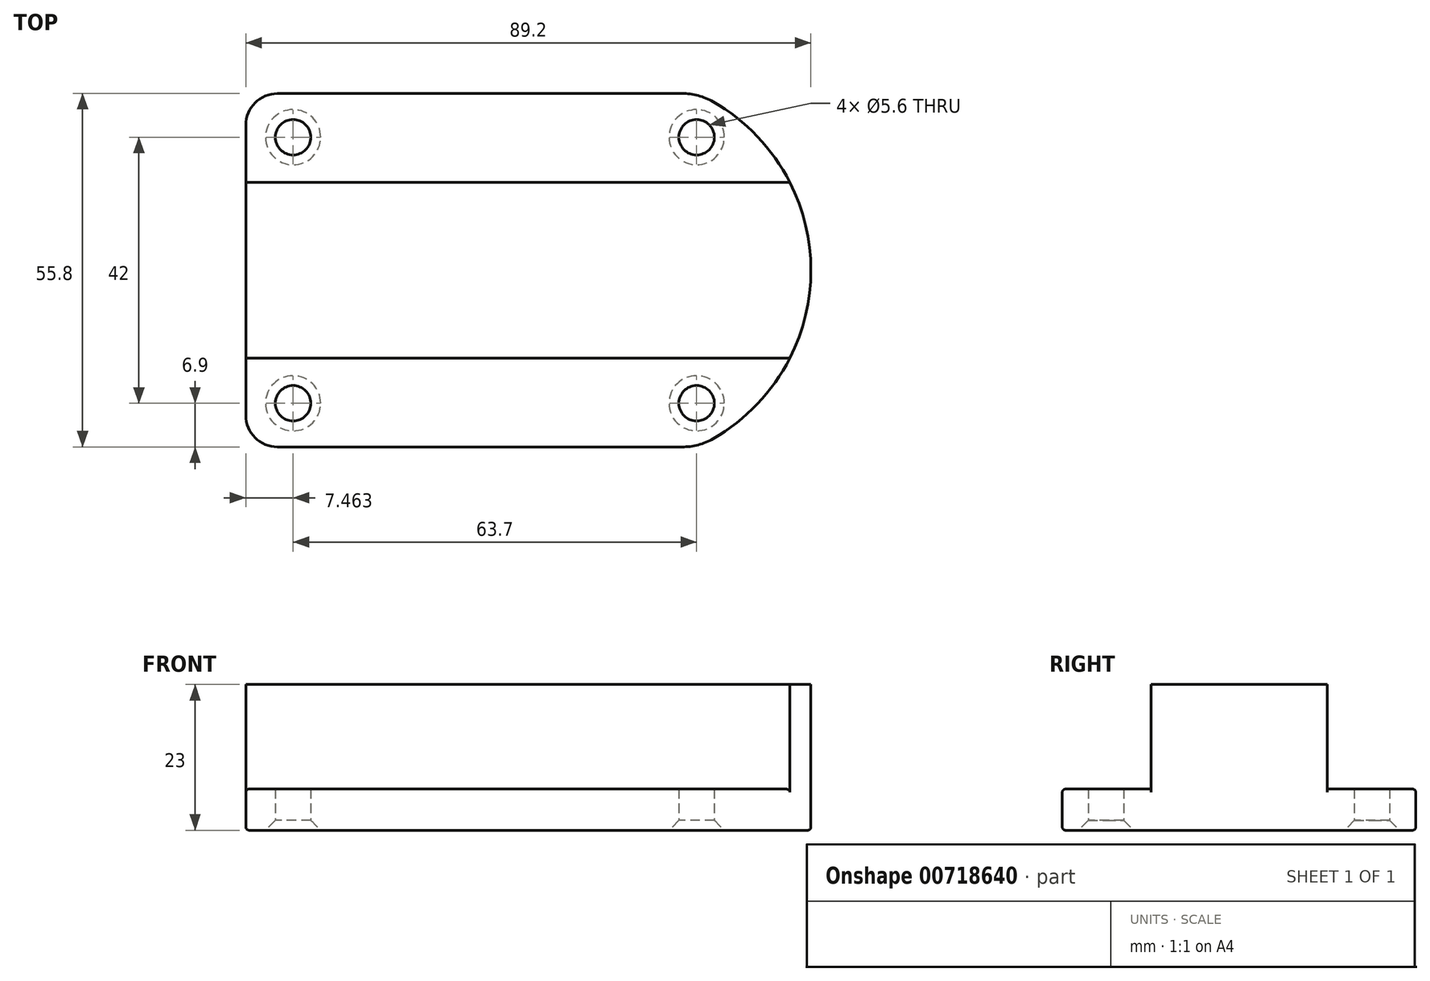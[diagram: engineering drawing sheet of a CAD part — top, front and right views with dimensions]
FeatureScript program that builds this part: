
annotation { "Feature Type Name" : "Feature", "Feature Type Description" : "" }
export const myFeature = defineFeature(function(context is Context, id is Id, definition is map)
    precondition{}
    {
        {
            var Q0;
            Q0=qCreatedBy(makeId("Top.planeOp"),FACE);
            var sketch = newSketch(context, id + "F0", { "sketchPlane" : qUnion([Q0])});
            skLineSegment(sketch, "E0.bottom", {"start": v(-38.88, -28.9) * mm, "end": v(-38.88, 16.9) * mm});
            skLineSegment(sketch, "E0.left", {"start": v(-33.88, -33.9) * mm, "end": v(29.94, -33.9) * mm});
            skLineSegment(sketch, "E0.right", {"start": v(-33.88, 21.9) * mm, "end": v(29.94, 21.9) * mm});
            skArc(sketch, "E1", {"start": v(34.9, -32.58) * mm, "mid": v(50.32, -6) * mm, "end": v(34.9, 20.58) * mm});
            skPoint(sketch, "E2.visualSharp", {"position": v(32.32, 21.9) * mm});
            skArc(sketch, "E2.filletArc", {"start": v(34.9, 20.58) * mm, "mid": v(32.51, 21.56) * mm, "end": v(29.94, 21.9) * mm});
            skPoint(sketch, "E3.visualSharp", {"position": v(32.32, -33.9) * mm});
            skArc(sketch, "E3.filletArc", {"start": v(29.94, -33.9) * mm, "mid": v(32.51, -33.56) * mm, "end": v(34.9, -32.58) * mm});
            skCircle(sketch, "E4", {"center": v(-31.42, 15) * mm, "radius": 2.8 * mm});
            skCircle(sketch, "E5", {"center": v(-31.42, -27) * mm, "radius": 2.8 * mm});
            skCircle(sketch, "E6", {"center": v(32.28, -27) * mm, "radius": 2.8 * mm});
            skCircle(sketch, "E7", {"center": v(32.28, 15) * mm, "radius": 2.8 * mm});
            skPoint(sketch, "E8.visualSharp", {"position": v(-38.88, 21.9) * mm});
            skArc(sketch, "E8.filletArc", {"start": v(-33.88, 21.9) * mm, "mid": v(-37.41, 20.44) * mm, "end": v(-38.88, 16.9) * mm});
            skPoint(sketch, "E9.visualSharp", {"position": v(-38.88, -33.9) * mm});
            skArc(sketch, "E9.filletArc", {"start": v(-38.88, -28.9) * mm, "mid": v(-37.41, -32.44) * mm, "end": v(-33.88, -33.9) * mm});
            skSolve(sketch);
        }
        {
            var Q0;
            Q0=qSketchRegion(id+"F0",true);
            extrude(context, id + "F1", {"entities" : qUnion([Q0]), "depth" : 6.5 * mm, "offsetDistance" : 25 * mm});
        }
        {
            var Q0;
            Q0=makeQuery(id+"F1.opExtrude","CAP_FACE",FACE,{"disambiguationData":[OSD([sQuery(id+"F0.wireOp",EDGE,"E0.bottom"),sQuery(id+"F0.wireOp",EDGE,"E0.left"),sQuery(id+"F0.wireOp",EDGE,"E0.right"),sQuery(id+"F0.wireOp",EDGE,"E1"),sQuery(id+"F0.wireOp",EDGE,"E2.filletArc"),sQuery(id+"F0.wireOp",EDGE,"E3.filletArc"),sQuery(id+"F0.wireOp",EDGE,"E4"),sQuery(id+"F0.wireOp",EDGE,"E5"),sQuery(id+"F0.wireOp",EDGE,"E6"),sQuery(id+"F0.wireOp",EDGE,"E7")])],"isStart":false});
            var sketch = newSketch(context, id + "F2", { "sketchPlane" : qUnion([Q0])});
            skLineSegment(sketch, "E10", {"start": v(-38.88, -6) * mm, "end": v(-38.88, 7.9) * mm});
            skLineSegment(sketch, "E11", {"start": v(-38.88, -6) * mm, "end": v(-38.88, -19.9) * mm});
            skLineSegment(sketch, "E12.bottom", {"start": v(-38.88, 7.9) * mm, "end": v(46.99, 7.9) * mm});
            skLineSegment(sketch, "E12.top", {"start": v(-38.88, -19.9) * mm, "end": v(46.99, -19.9) * mm});
            skLineSegment(sketch, "E12.left", {"start": v(-38.88, 7.9) * mm, "end": v(-38.88, -19.9) * mm});
            skArc(sketch, "E13", {"start": v(46.99, -19.9) * mm, "mid": v(50.32, -6) * mm, "end": v(46.99, 7.9) * mm});
            skSolve(sketch);
        }
        {
            var Q0;
            Q0=qSketchRegion(id+"F2",true);
            extrude(context, id + "F3", {"entities" : qUnion([Q0]), "operationType" : NewBodyOperationType.ADD, "depth" : 16.5 * mm, "offsetDistance" : 25 * mm});
        }
        {
            var Q0;
            Q0=makeQuery(id+"F1.opExtrude","CAP_EDGE",EDGE,{"disambiguationData":[OSD([sQuery(id+"F0.wireOp",EDGE,"E0.right")])],"isStart":true});
            var Q1;
            Q1=makeQuery(id+"F1.opExtrude","CAP_EDGE",EDGE,{"disambiguationData":[OSD([sQuery(id+"F0.wireOp",EDGE,"E8.filletArc")])],"isStart":true});
            var Q2;
            Q2=makeQuery(id+"F1.opExtrude","CAP_EDGE",EDGE,{"disambiguationData":[OSD([sQuery(id+"F0.wireOp",EDGE,"E0.right")])],"isStart":false});
            var Q3;
            Q3=makeQuery(id+"F1.opExtrude","CAP_EDGE",EDGE,{"disambiguationData":[OSD([sQuery(id+"F0.wireOp",EDGE,"E0.left")])],"isStart":false});
            var Q4;
            Q4=makeQuery(id+"F1.opExtrude","CAP_EDGE",EDGE,{"disambiguationData":[OSD([sQuery(id+"F0.wireOp",EDGE,"E0.left")])],"isStart":true});
            var Q5;
            Q5=makeQuery(id+"F1.opExtrude","CAP_EDGE",EDGE,{"disambiguationData":[OSD([sQuery(id+"F0.wireOp",EDGE,"E1")])],"isStart":true});
            var Q6;
            Q6=makeQuery(id+"F1.opExtrude","CAP_EDGE",EDGE,{"disambiguationData":[OSD([sQuery(id+"F0.wireOp",EDGE,"E0.bottom")])],"isStart":true});
            fillet(context, id + "F4", {"entities" : qUnion([Q0, Q1, Q2, Q3, Q4, Q5, Q6]), "radius" : 0.5 * mm, "tangentPropagation" : true, "allowEdgeOverflow" : false});
        }
        {
            var Q0;
            Q0=makeQuery(id+"F1.opExtrude","CAP_EDGE",EDGE,{"disambiguationData":[OSD([sQuery(id+"F0.wireOp",EDGE,"E4")])],"isStart":true});
            var Q1;
            Q1=makeQuery(id+"F1.opExtrude","CAP_EDGE",EDGE,{"disambiguationData":[OSD([sQuery(id+"F0.wireOp",EDGE,"E5")])],"isStart":true});
            var Q2;
            Q2=makeQuery(id+"F1.opExtrude","CAP_EDGE",EDGE,{"disambiguationData":[OSD([sQuery(id+"F0.wireOp",EDGE,"E6")])],"isStart":true});
            var Q3;
            Q3=makeQuery(id+"F1.opExtrude","CAP_EDGE",EDGE,{"disambiguationData":[OSD([sQuery(id+"F0.wireOp",EDGE,"E7")])],"isStart":true});
            chamfer(context, id + "F5", {"entities" : qUnion([Q0, Q1, Q2, Q3]), "width" : 1.56 * mm, "tangentPropagation" : true});
        }
    });
